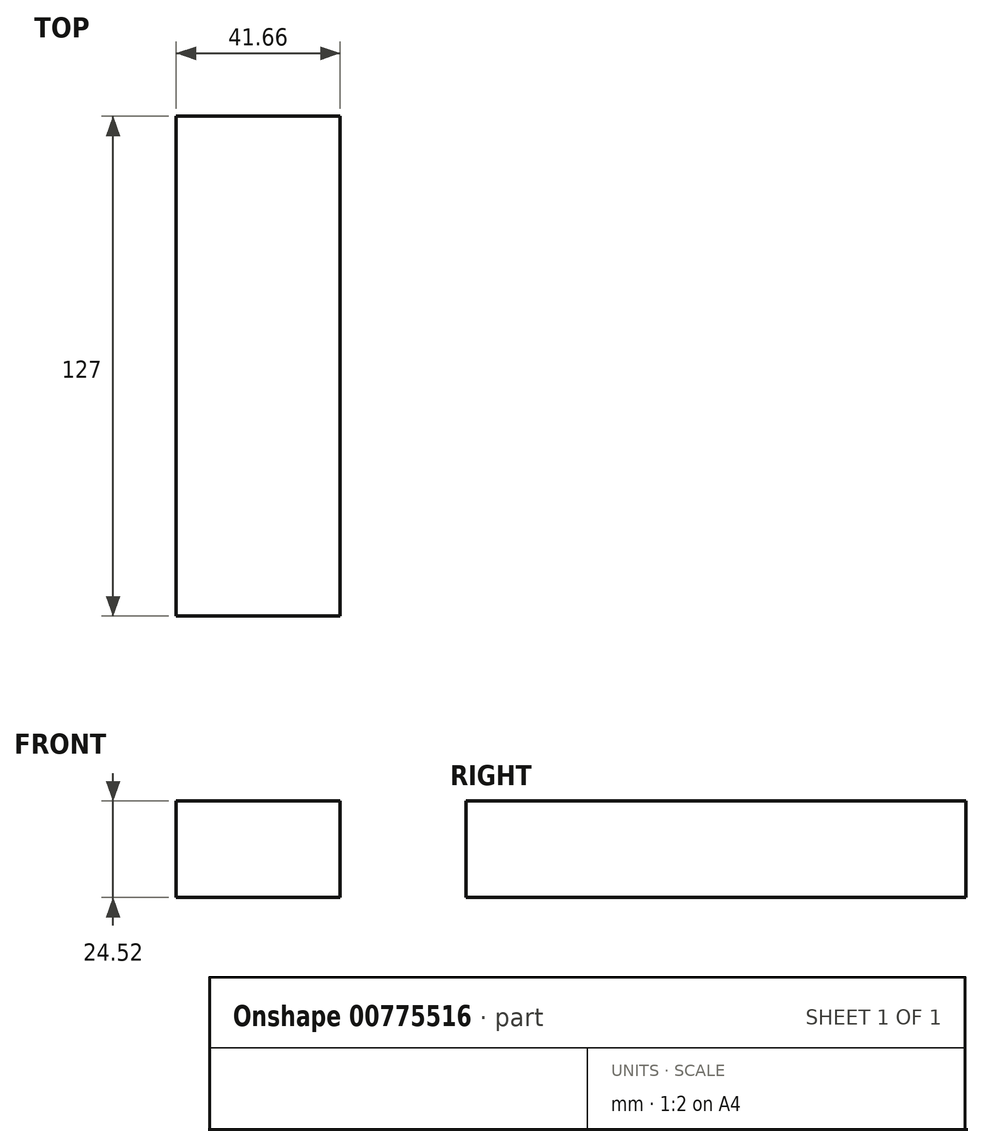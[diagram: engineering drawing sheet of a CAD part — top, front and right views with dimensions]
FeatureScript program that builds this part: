
annotation { "Feature Type Name" : "Feature", "Feature Type Description" : "" }
export const myFeature = defineFeature(function(context is Context, id is Id, definition is map)
    precondition{}
    {
        {
            var Q0;
            Q0=qCreatedBy(makeId("Front.planeOp"),FACE);
            var sketch = newSketch(context, id + "F0", { "sketchPlane" : qUnion([Q0])});
            skLineSegment(sketch, "E0.bottom", {"start": v(-58.9, 38.44) * mm, "end": v(-17.24, 38.44) * mm});
            skLineSegment(sketch, "E0.top", {"start": v(-58.9, 13.92) * mm, "end": v(-17.24, 13.92) * mm});
            skLineSegment(sketch, "E0.left", {"start": v(-58.9, 38.44) * mm, "end": v(-58.9, 13.92) * mm});
            skLineSegment(sketch, "E0.right", {"start": v(-17.24, 38.44) * mm, "end": v(-17.24, 13.92) * mm});
            skSolve(sketch);
        }
        {
            var Q0;
            Q0=makeQuery(id+"F0.imprint","IMPRINT",FACE,{"disambiguationData":[TD([[makeQuery(id+"F0.imprint","IMPRINT",EDGE,{"derivedFrom":sQuery(id+"F0.wireOp",EDGE,"E0.bottom")}),-1.0]])]});
            extrude(context, id + "F1", {"entities" : qUnion([Q0]), "depth" : 127 * mm, "offsetDistance" : 25.4 * mm});
        }
    });
